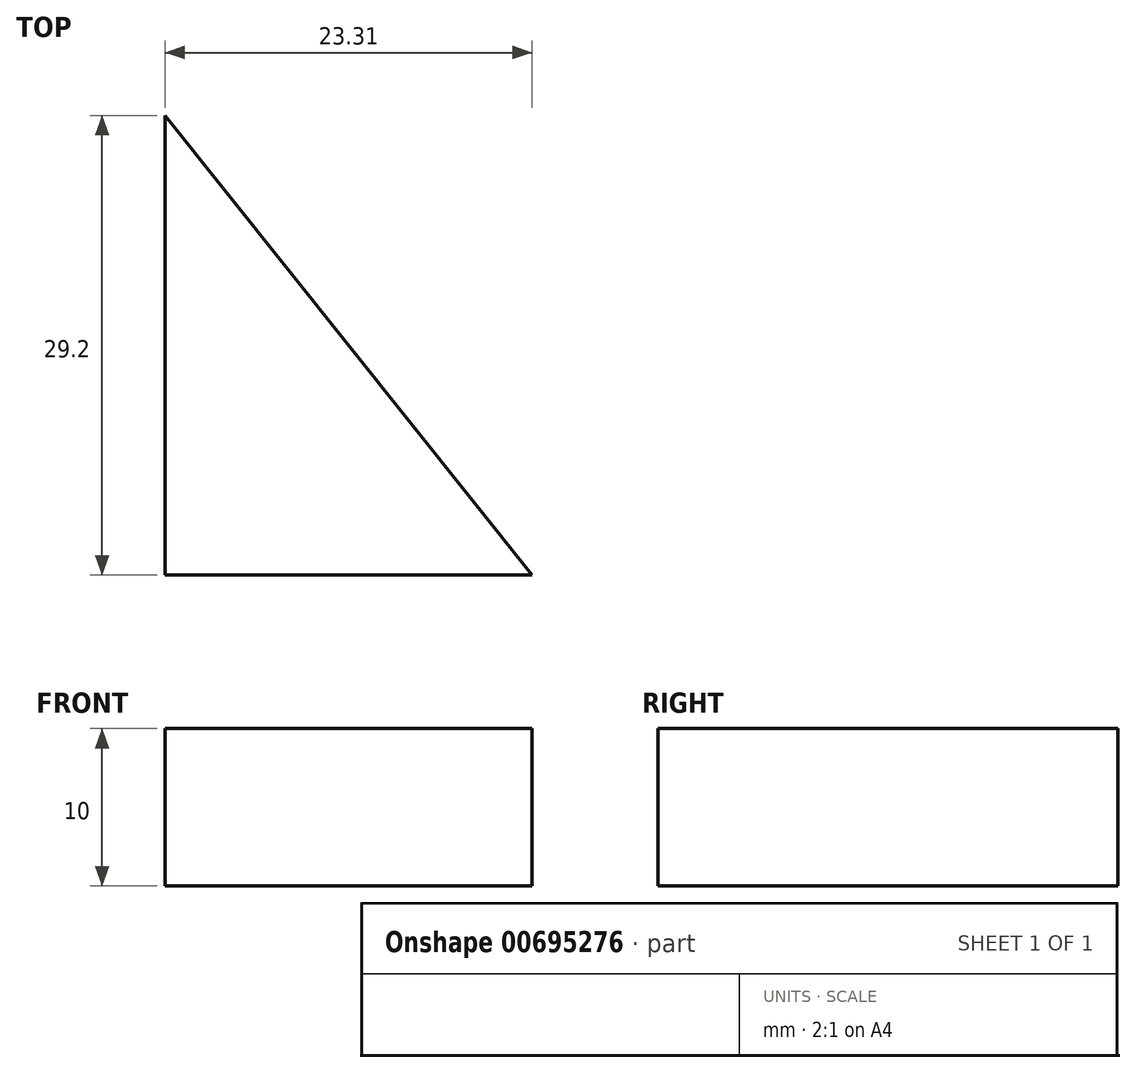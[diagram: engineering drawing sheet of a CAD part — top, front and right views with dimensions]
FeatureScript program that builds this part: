
annotation { "Feature Type Name" : "Feature", "Feature Type Description" : "" }
export const myFeature = defineFeature(function(context is Context, id is Id, definition is map)
    precondition{}
    {
        {
            var Q0;
            Q0=qCreatedBy(makeId("Top.planeOp"),FACE);
            var sketch = newSketch(context, id + "F0", { "sketchPlane" : qUnion([Q0])});
            skLineSegment(sketch, "E0", {"start": v(-13.45, 18.7) * mm, "end": v(-13.45, -10.5) * mm});
            skLineSegment(sketch, "E1", {"start": v(-13.45, -10.5) * mm, "end": v(9.86, -10.5) * mm});
            skLineSegment(sketch, "E2", {"start": v(9.86, -10.5) * mm, "end": v(-13.45, 18.7) * mm});
            skSolve(sketch);
        }
        {
            var Q0;
            Q0 = qSketchRegion(id + "F0", true);
            extrude(context, id + "F1", {"entities" : qUnion([Q0]), "depth" : 10 * mm, "offsetDistance" : 25 * mm});
        }
    });
